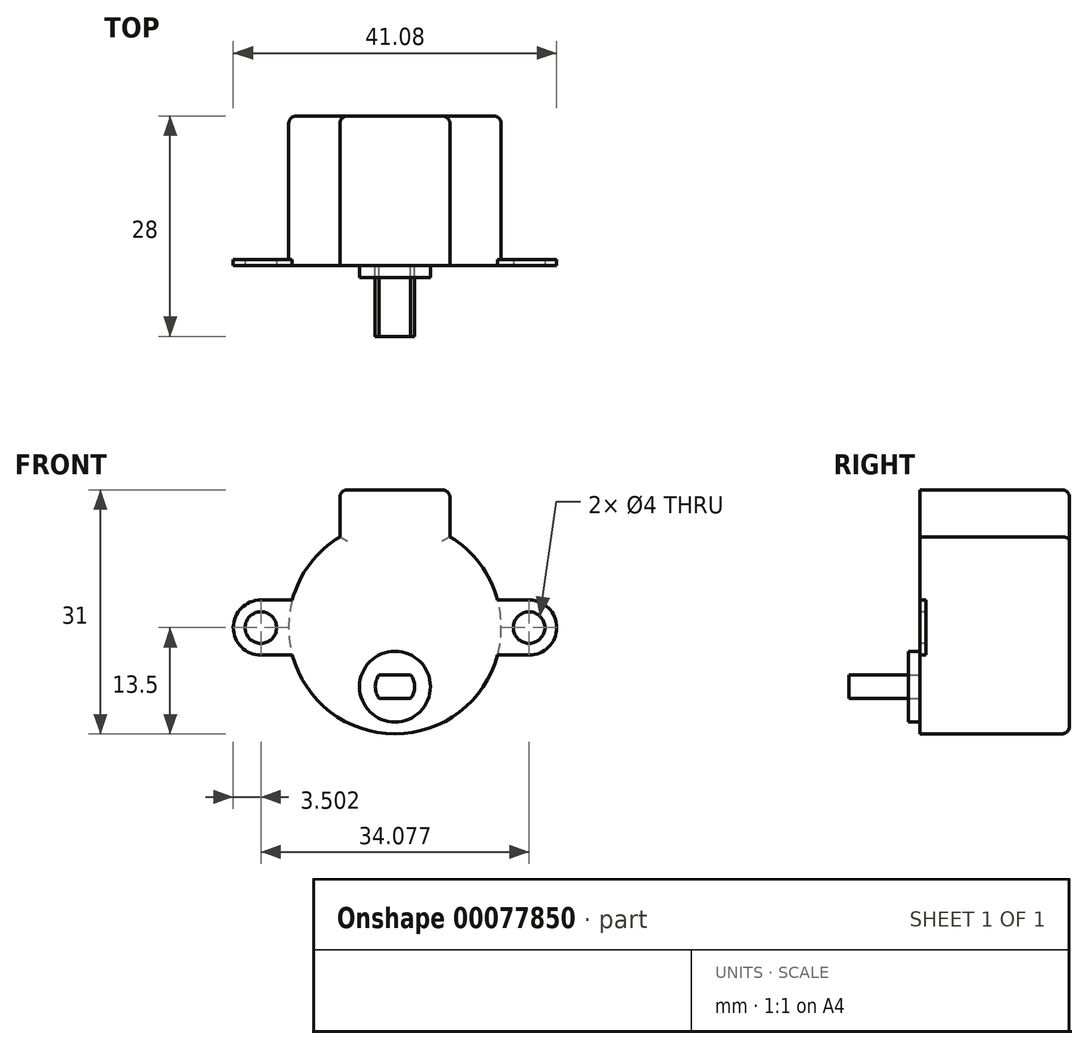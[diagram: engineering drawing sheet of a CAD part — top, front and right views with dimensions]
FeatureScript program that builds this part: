
annotation { "Feature Type Name" : "Feature", "Feature Type Description" : "" }
export const myFeature = defineFeature(function(context is Context, id is Id, definition is map)
    precondition{}
    {
        {
            var Q0;
            Q0=qCreatedBy(makeId("Front.planeOp"),FACE);
            var sketch = newSketch(context, id + "F0", { "sketchPlane" : qUnion([Q0])});
            skCircle(sketch, "E0", {"center": v(0, 0) * mm, "radius": 13.5 * mm});
            skLineSegment(sketch, "E1", {"start": v(17.04, 3.5) * mm, "end": v(13.04, 3.5) * mm});
            skLineSegment(sketch, "E2", {"start": v(17.04, -3.5) * mm, "end": v(13.04, -3.5) * mm});
            skArc(sketch, "E3", {"start": v(17.04, 3.5) * mm, "mid": v(20.54, 0) * mm, "end": v(17.04, -3.5) * mm});
            skLineSegment(sketch, "E4", {"start": v(-13.04, 3.5) * mm, "end": v(-17.04, 3.5) * mm});
            skLineSegment(sketch, "E5", {"start": v(-13.04, -3.5) * mm, "end": v(-17.04, -3.5) * mm});
            skArc(sketch, "E6", {"start": v(-17.04, 3.5) * mm, "mid": v(-20.54, 0) * mm, "end": v(-17.04, -3.5) * mm});
            skLineSegment(sketch, "E7", {"start": v(-7, 11.54) * mm, "end": v(-7, 17.5) * mm});
            skLineSegment(sketch, "E8", {"start": v(-7, 17.5) * mm, "end": v(7, 17.5) * mm});
            skLineSegment(sketch, "E9", {"start": v(7, 17.5) * mm, "end": v(7, 11.54) * mm});
            skPoint(sketch, "E10", {"position": v(0, 17.5) * mm});
            skCircle(sketch, "E11", {"center": v(0, -7.5) * mm, "radius": 4.5 * mm});
            skLineSegment(sketch, "E12", {"start": v(-2, -6) * mm, "end": v(2, -6) * mm});
            skLineSegment(sketch, "E13", {"start": v(-2, -9) * mm, "end": v(2, -9) * mm});
            skArc(sketch, "E14", {"start": v(2, -6) * mm, "mid": v(2.5, -7.5) * mm, "end": v(2, -9) * mm});
            skArc(sketch, "E15", {"start": v(-2, -9) * mm, "mid": v(-2.5, -7.5) * mm, "end": v(-2, -6) * mm});
            skSolve(sketch);
        }
        {
            var Q0;
            Q0=makeQuery(id+"F0.imprint","IMPRINT",FACE,{"disambiguationData":[TD([[makeQuery(id+"F0.imprint","IMPRINT",EDGE,{"derivedFrom":sQuery(id+"F0.wireOp",EDGE,"E11")}),-1.0]])]});
            var Q1;
            Q1=makeQuery(id+"F0.imprint","IMPRINT",FACE,{"disambiguationData":[TD([[makeQuery(id+"F0.imprint","IMPRINT",EDGE,{"derivedFrom":sQuery(id+"F0.wireOp",EDGE,"E11")}),1.0]])]});
            var Q2;
            Q2=makeQuery(id+"F0.imprint","IMPRINT",FACE,{"disambiguationData":[TD([[makeQuery(id+"F0.imprint","IMPRINT",EDGE,{"derivedFrom":sQuery(id+"F0.wireOp",EDGE,"E12")}),-1.0]])]});
            var Q3;
            {var subQ0=sQuery(id+"F0.wireOp",EDGE,"E7");Q3=makeQuery(id+"F0.imprint","IMPRINT",FACE,{"disambiguationData":[TD([[makeQuery(id+"F0.imprint","IMPRINT",EDGE,{"derivedFrom":subQ0}),-1.0]])]});}
            extrude(context, id + "F1", {"entities" : qUnion([Q0, Q1, Q2, Q3]), "oppositeDirection" : true, "depth" : 19 * mm});
        }
        {
            var Q0;
            {var subQ0=sQuery(id+"F0.wireOp",EDGE,"E4");Q0=makeQuery(id+"F0.imprint","IMPRINT",FACE,{"disambiguationData":[TD([[makeQuery(id+"F0.imprint","IMPRINT",EDGE,{"derivedFrom":subQ0}),1.0]])]});}
            var Q1;
            {var subQ0=sQuery(id+"F0.wireOp",EDGE,"E1");Q1=makeQuery(id+"F0.imprint","IMPRINT",FACE,{"disambiguationData":[TD([[makeQuery(id+"F0.imprint","IMPRINT",EDGE,{"derivedFrom":subQ0}),1.0]])]});}
            extrude(context, id + "F2", {"entities" : qUnion([Q0, Q1]), "operationType" : NewBodyOperationType.ADD, "oppositeDirection" : true, "depth" : 0.75 * mm});
        }
        {
            var Q0;
            Q0=makeQuery(id+"F0.imprint","IMPRINT",FACE,{"disambiguationData":[TD([[makeQuery(id+"F0.imprint","IMPRINT",EDGE,{"derivedFrom":sQuery(id+"F0.wireOp",EDGE,"E11")}),1.0]])]});
            extrude(context, id + "F3", {"entities" : qUnion([Q0]), "operationType" : NewBodyOperationType.ADD, "depth" : 1.5 * mm});
        }
        {
            var Q0;
            Q0=makeQuery(id+"F0.imprint","IMPRINT",FACE,{"disambiguationData":[TD([[makeQuery(id+"F0.imprint","IMPRINT",EDGE,{"derivedFrom":sQuery(id+"F0.wireOp",EDGE,"E12")}),-1.0]])]});
            extrude(context, id + "F4", {"entities" : qUnion([Q0]), "depth" : 9 * mm});
        }
        {
            var Q0;
            Q0=sQuery(id+"F0.wireOp",VERTEX,"E6.center");
            var Q1;
            Q1=sQuery(id+"F0.wireOp",VERTEX,"E3.center");
            var Q2;
            Q2=makeQuery(id+"F1.opExtrude","SWEPT_BODY",BODY,{"disambiguationData":[OSD([sQuery(id+"F0.wireOp",EDGE,"E0"),sQuery(id+"F0.wireOp",EDGE,"E7"),sQuery(id+"F0.wireOp",EDGE,"E8"),sQuery(id+"F0.wireOp",EDGE,"E9")])]});
            hole(context, id + "F5", {"style" : HoleStyle.SIMPLE, "endStyle" : HoleEndStyle.THROUGH, "holeDiameter" : 4 * mm, "locations" : qUnion([Q0, Q1]), "scope" : qUnion([Q2]), "isTappedThrough" : true});
        }
        {
            var Q0;
            Q0=makeQuery(id+"F1.opExtrude","CAP_EDGE",EDGE,{"disambiguationData":[OSD([sQuery(id+"F0.wireOp",EDGE,"E0")])],"isStart":false});
            var Q1;
            Q1=makeQuery(id+"F1.opExtrude","CAP_EDGE",EDGE,{"disambiguationData":[OSD([sQuery(id+"F0.wireOp",EDGE,"E9")])],"isStart":false});
            var Q2;
            Q2=makeQuery(id+"F1.opExtrude","CAP_EDGE",EDGE,{"disambiguationData":[OSD([sQuery(id+"F0.wireOp",EDGE,"E8")])],"isStart":false});
            var Q3;
            Q3=makeQuery(id+"F1.opExtrude","CAP_EDGE",EDGE,{"disambiguationData":[OSD([sQuery(id+"F0.wireOp",EDGE,"E7")])],"isStart":false});
            var Q4;
            Q4=makeQuery(id+"F1.opExtrude","SWEPT_EDGE",EDGE,{"disambiguationData":[OSD([sQuery(id+"F0.wireOp",EDGE,"E8"),sQuery(id+"F0.wireOp",EDGE,"E9")])]});
            var Q5;
            Q5=makeQuery(id+"F1.opExtrude","SWEPT_EDGE",EDGE,{"disambiguationData":[OSD([sQuery(id+"F0.wireOp",EDGE,"E7"),sQuery(id+"F0.wireOp",EDGE,"E8")])]});
            fillet(context, id + "F6", {"entities" : qUnion([Q0, Q1, Q2, Q3, Q4, Q5]), "radius" : 1 * mm, "tangentPropagation" : true, "allowEdgeOverflow" : false});
        }
    });
